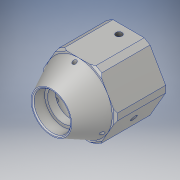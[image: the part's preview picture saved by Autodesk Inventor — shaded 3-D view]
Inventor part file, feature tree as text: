
AUTODESK INVENTOR PART (.ipt)
format: ipt  version: 2019 (Build 230136000, 136)  size: 251,392 bytes
history: native  units: mm
features: sketch x7, chamfer x4, hole x4, extrude x2, other x1, pattern_circular x1, mirror x1, projected_geometry x1
ambient origin geometry x8: Origin, YZ Plane, XZ Plane, XY Plane, X Axis, Y Axis, Z Axis, Center Point
bodies: Solide1 (feature_tree)
feature tree (21):
  other  "Révolution1"
  extrude  "Extrusion1"  Depth=16.0mm
  chamfer  "Chanfrein1"  Distance=22.0mm
  chamfer  "Chanfrein2"  Distance=35.0mm
  hole  "Perçage1"  [1 undecoded]
  hole  "Perçage2"  [1 undecoded]
  extrude  "Extrusion2"  TaperAngle=90.0deg  [1 undecoded]
  hole  "Perçage3"  [1 undecoded]
  pattern_circular  "Réseau circulaire1"  Angle=45.0deg  [1 undecoded]
  chamfer  "Chanfrein4"  Distance=2.0mm Angle=45.0deg
  chamfer  "Chanfrein5"  Distance=8.0mm
  hole  "Perçage4"  [1 undecoded]
  mirror  "Symétrie1"
  sketch  "Esquisse1"
  sketch  "Esquisse2"
  sketch  "Esquisse3"
  sketch  "Esquisse4"
  sketch  "Esquisse5"
  projected_geometry  "Boucle projetée1"
  sketch  "Esquisse6"
  sketch  "Esquisse7"
note: 6 required parameter values undecoded (feature->parameter linkage not recoverable at this tier; creation-order binding heuristic only, values carry confidence <= 0.55)
